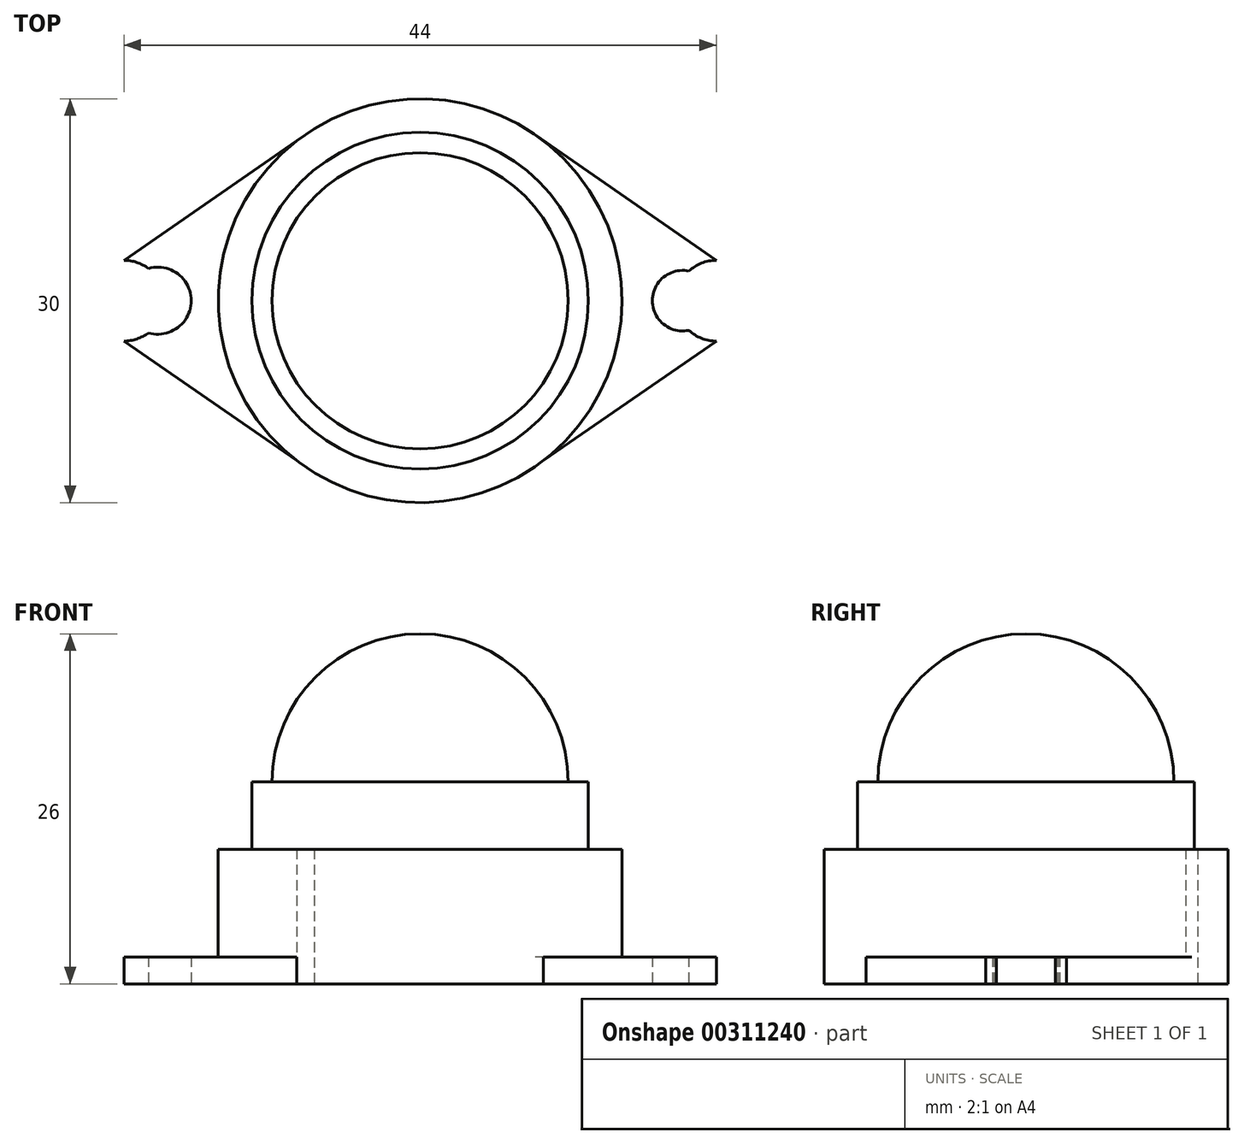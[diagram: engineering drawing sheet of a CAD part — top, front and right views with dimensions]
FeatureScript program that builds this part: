
annotation { "Feature Type Name" : "Feature", "Feature Type Description" : "" }
export const myFeature = defineFeature(function(context is Context, id is Id, definition is map)
    precondition{}
    {
        {
            var Q0;
            Q0=qCreatedBy(makeId("Top.planeOp"),FACE);
            var sketch = newSketch(context, id + "F0", { "sketchPlane" : qUnion([Q0])});
            skLineSegment(sketch, "E0", {"start": v(0, 0) * mm, "end": v(25, 0) * mm});
            skLineSegment(sketch, "E1", {"start": v(0, 0) * mm, "end": v(-25, 0) * mm});
            skLineSegment(sketch, "E2", {"start": v(25, 0) * mm, "end": v(22, 0) * mm});
            skLineSegment(sketch, "E3", {"start": v(-25, 0) * mm, "end": v(-22, 0) * mm});
            skLineSegment(sketch, "E4", {"start": v(-22, 0) * mm, "end": v(-19.5, 0) * mm});
            skLineSegment(sketch, "E5", {"start": v(22, 0) * mm, "end": v(19.5, 0) * mm});
            skCircle(sketch, "E6", {"center": v(0, 0) * mm, "radius": 15 * mm});
            skCircle(sketch, "E7", {"center": v(-19.5, 0) * mm, "radius": 2.5 * mm});
            skCircle(sketch, "E8", {"center": v(19.5, 0) * mm, "radius": 2.25 * mm});
            skCircle(sketch, "E9", {"center": v(-22, 0) * mm, "radius": 3 * mm});
            skCircle(sketch, "E10", {"center": v(22, 0) * mm, "radius": 3 * mm});
            skLineSegment(sketch, "E11", {"start": v(-22, 3) * mm, "end": v(-7.87, 12.77) * mm});
            skLineSegment(sketch, "E12", {"start": v(-22, -3) * mm, "end": v(-7.87, -12.77) * mm});
            skLineSegment(sketch, "E13", {"start": v(22, 3) * mm, "end": v(7.91, 12.77) * mm});
            skLineSegment(sketch, "E14", {"start": v(22, -3) * mm, "end": v(7.91, -12.74) * mm});
            skSolve(sketch);
        }
        {
            var Q0;
            {var subQ2=sQuery(id+"F0.wireOp",EDGE,"E0");var subQ4=sQuery(id+"F0.wireOp",EDGE,"E1");var subQ5=makeQuery(id+"F0.imprint","INTERSECT",VERTEX,{"derivedFrom":[subQ2,subQ4]});Q0=makeQuery(id+"F0.imprint","IMPRINT",FACE,{"disambiguationData":[TD([[makeQuery(id+"F0.imprint","IMPRINT",EDGE,{"disambiguationData":[TD([[subQ5,-1.0]])],"derivedFrom":subQ2}),1.0]])]});}
            var sketch = newSketch(context, id + "F1", { "sketchPlane" : qUnion([Q0])});
            skCircle(sketch, "E15", {"center": v(0, 0) * mm, "radius": 15 * mm});
            skSolve(sketch);
        }
        {
            var Q0;
            {var subQ4=sQuery(id+"F0.wireOp",EDGE,"E1");var subQ5=sQuery(id+"F0.wireOp",EDGE,"E0");var subQ6=makeQuery(id+"F0.imprint","INTERSECT",VERTEX,{"derivedFrom":[subQ5,subQ4]});var subQ9=makeQuery(id+"F0.imprint","IMPRINT",EDGE,{"disambiguationData":[TD([[subQ6,-1.0]])],"derivedFrom":subQ5});Q0=makeQuery(id+"F1.imprint","IMPRINT",FACE,{"disambiguationData":[TD([[makeQuery(id+"F1.imprint","IMPRINT",EDGE,{"derivedFrom":subQ9}),1.0]])]});}
            var Q1;
            {var subQ1=sQuery(id+"F0.wireOp",EDGE,"E1");var subQ2=sQuery(id+"F0.wireOp",EDGE,"E0");var subQ3=makeQuery(id+"F0.imprint","INTERSECT",VERTEX,{"derivedFrom":[subQ2,subQ1]});var subQ5=makeQuery(id+"F0.imprint","IMPRINT",EDGE,{"disambiguationData":[TD([[subQ3,-1.0]])],"derivedFrom":subQ2});Q1=makeQuery(id+"F1.imprint","IMPRINT",FACE,{"disambiguationData":[TD([[makeQuery(id+"F1.imprint","IMPRINT",EDGE,{"derivedFrom":subQ5}),-1.0]])]});}
            extrude(context, id + "F2", {"entities" : qUnion([Q0, Q1]), "depth" : 10 * mm});
        }
        {
            var Q0;
            Q0=makeQuery(id+"F2.opExtrude","CAP_FACE",FACE,{"disambiguationData":[OSD([sQuery(id+"F0.wireOp",EDGE,"E11"),sQuery(id+"F1.wireOp",EDGE,"E15")])],"isStart":false});
            var sketch = newSketch(context, id + "F3", { "sketchPlane" : qUnion([Q0])});
            skCircle(sketch, "E16", {"center": v(0, 0) * mm, "radius": 12.5 * mm});
            skSolve(sketch);
        }
        {
            var Q0;
            Q0=makeQuery(id+"F3.imprint","IMPRINT",FACE,{"disambiguationData":[TD([[makeQuery(id+"F3.imprint","IMPRINT",EDGE,{"derivedFrom":sQuery(id+"F3.wireOp",EDGE,"E16")}),1.0]])]});
            extrude(context, id + "F4", {"entities" : qUnion([Q0]), "operationType" : NewBodyOperationType.ADD, "depth" : 5 * mm});
        }
        {
            var Q0;
            Q0=makeQuery(id+"F4.opExtrude","CAP_FACE",FACE,{"disambiguationData":[OSD([sQuery(id+"F3.wireOp",EDGE,"E16")])],"isStart":false});
            var sketch = newSketch(context, id + "F5", { "sketchPlane" : qUnion([Q0])});
            skCircle(sketch, "E17", {"center": v(0, 0) * mm, "radius": 11 * mm});
            skLineSegment(sketch, "E18", {"start": v(0, -11) * mm, "end": v(0, 11) * mm});
            skSolve(sketch);
        }
        {
            var Q0;
            {var subQ0=sQuery(id+"F5.wireOp",EDGE,"E18");Q0=makeQuery(id+"F5.imprint","IMPRINT",FACE,{"disambiguationData":[TD([[makeQuery(id+"F5.imprint","IMPRINT",EDGE,{"derivedFrom":subQ0}),1.0]])]});}
            var Q1;
            Q1=sQuery(id+"F5.wireOp",EDGE,"E18");
            revolve(context, id + "F6", {"operationType" : NewBodyOperationType.ADD, "entities" : qUnion([Q0]), "axis" : qUnion([Q1]), "revolveType" : RevolveType.FULL});
        }
        {
            var Q0;
            {var subQ5=sQuery(id+"F0.wireOp",EDGE,"E6");var subQ7=sQuery(id+"F0.wireOp",EDGE,"E1");var subQ8=makeQuery(id+"F0.imprint","INTERSECT",VERTEX,{"derivedFrom":[subQ7,subQ5]});Q0=makeQuery(id+"F0.imprint","IMPRINT",FACE,{"disambiguationData":[TD([[makeQuery(id+"F0.imprint","IMPRINT",EDGE,{"disambiguationData":[TD([[subQ8,-1.0]])],"derivedFrom":subQ7}),1.0]])]});}
            var Q1;
            {var subQ5=sQuery(id+"F0.wireOp",EDGE,"E0");var subQ7=sQuery(id+"F0.wireOp",EDGE,"E6");var subQ9=makeQuery(id+"F0.imprint","INTERSECT",VERTEX,{"derivedFrom":[subQ5,subQ7]});Q1=makeQuery(id+"F0.imprint","IMPRINT",FACE,{"disambiguationData":[TD([[makeQuery(id+"F0.imprint","IMPRINT",EDGE,{"disambiguationData":[TD([[subQ9,-1.0]])],"derivedFrom":subQ5}),-1.0]])]});}
            var Q2;
            {var subQ6=sQuery(id+"F0.wireOp",EDGE,"E2");Q2=makeQuery(id+"F0.imprint","IMPRINT",FACE,{"disambiguationData":[TD([[makeQuery(id+"F0.imprint","IMPRINT",EDGE,{"derivedFrom":subQ6}),1.0]])]});}
            var Q3;
            {var subQ5=sQuery(id+"F0.wireOp",EDGE,"E0");var subQ7=sQuery(id+"F0.wireOp",EDGE,"E6");var subQ9=makeQuery(id+"F0.imprint","INTERSECT",VERTEX,{"derivedFrom":[subQ5,subQ7]});Q3=makeQuery(id+"F0.imprint","IMPRINT",FACE,{"disambiguationData":[TD([[makeQuery(id+"F0.imprint","IMPRINT",EDGE,{"disambiguationData":[TD([[subQ9,-1.0]])],"derivedFrom":subQ5}),1.0]])]});}
            var Q4;
            {var subQ1=sQuery(id+"F0.wireOp",EDGE,"E2");Q4=makeQuery(id+"F0.imprint","IMPRINT",FACE,{"disambiguationData":[TD([[makeQuery(id+"F0.imprint","IMPRINT",EDGE,{"derivedFrom":subQ1}),-1.0]])]});}
            var Q5;
            {var subQ5=sQuery(id+"F0.wireOp",EDGE,"E6");var subQ7=sQuery(id+"F0.wireOp",EDGE,"E1");var subQ9=makeQuery(id+"F0.imprint","INTERSECT",VERTEX,{"derivedFrom":[subQ7,subQ5]});Q5=makeQuery(id+"F0.imprint","IMPRINT",FACE,{"disambiguationData":[TD([[makeQuery(id+"F0.imprint","IMPRINT",EDGE,{"disambiguationData":[TD([[subQ9,-1.0]])],"derivedFrom":subQ7}),-1.0]])]});}
            var Q6;
            {var subQ4=sQuery(id+"F0.wireOp",EDGE,"E3");Q6=makeQuery(id+"F0.imprint","IMPRINT",FACE,{"disambiguationData":[TD([[makeQuery(id+"F0.imprint","IMPRINT",EDGE,{"derivedFrom":subQ4}),1.0]])]});}
            var Q7;
            {var subQ1=sQuery(id+"F0.wireOp",EDGE,"E3");Q7=makeQuery(id+"F0.imprint","IMPRINT",FACE,{"disambiguationData":[TD([[makeQuery(id+"F0.imprint","IMPRINT",EDGE,{"derivedFrom":subQ1}),-1.0]])]});}
            extrude(context, id + "F7", {"entities" : qUnion([Q0, Q1, Q2, Q3, Q4, Q5, Q6, Q7]), "operationType" : NewBodyOperationType.ADD, "depth" : 2 * mm});
        }
    });
